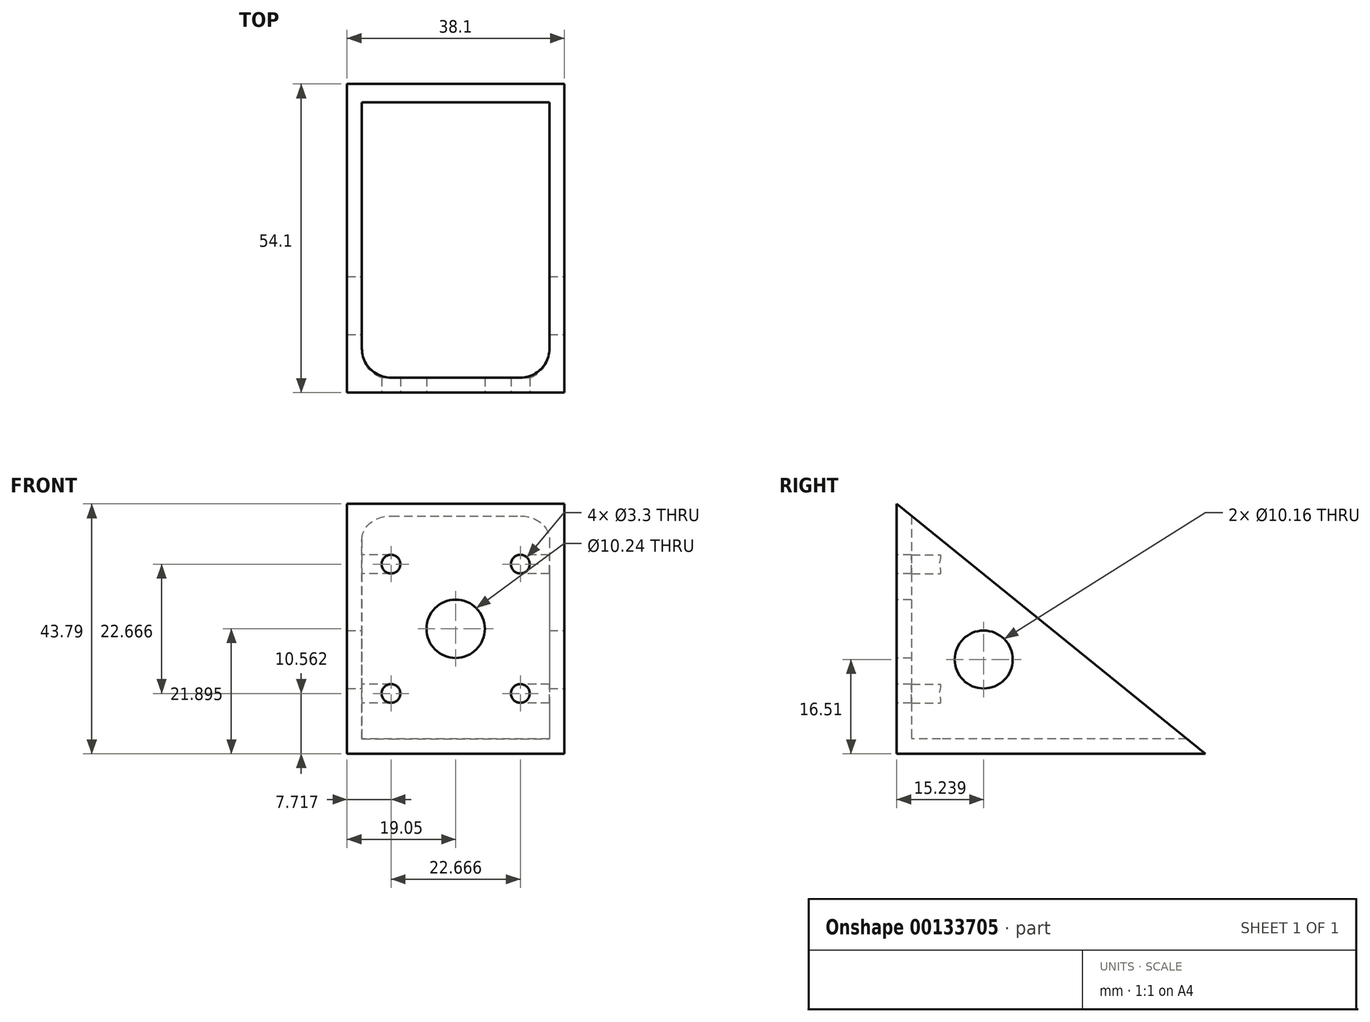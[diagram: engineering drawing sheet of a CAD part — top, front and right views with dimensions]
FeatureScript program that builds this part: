
annotation { "Feature Type Name" : "Feature", "Feature Type Description" : "" }
export const myFeature = defineFeature(function(context is Context, id is Id, definition is map)
    precondition{}
    {
        {
            var Q0;
            Q0=qCreatedBy(makeId("Top.planeOp"),FACE);
            var sketch = newSketch(context, id + "F0", { "sketchPlane" : qUnion([Q0])});
            skLineSegment(sketch, "E0.bottom", {"start": v(19.05, 27.05) * mm, "end": v(-19.05, 27.05) * mm});
            skLineSegment(sketch, "E0.top", {"start": v(19.05, -27.05) * mm, "end": v(-19.05, -27.05) * mm});
            skLineSegment(sketch, "E0.left", {"start": v(19.05, 27.05) * mm, "end": v(19.05, -27.05) * mm});
            skLineSegment(sketch, "E0.right", {"start": v(-19.05, 27.05) * mm, "end": v(-19.05, -27.05) * mm});
            skPoint(sketch, "E0.middle", {"position": v(0, 0) * mm});
            skSolve(sketch);
        }
        {
            var Q0;
            Q0 = qSketchRegion(id + "F0", true);
            extrude(context, id + "F1", {"entities" : qUnion([Q0]), "depth" : 2.6 * mm});
        }
        {
            var Q0;
            Q0=makeQuery(id+"F1.opExtrude","CAP_FACE",FACE,{"disambiguationData":[OSD([sQuery(id+"F0.wireOp",EDGE,"E0.bottom"),sQuery(id+"F0.wireOp",EDGE,"E0.top"),sQuery(id+"F0.wireOp",EDGE,"E0.left"),sQuery(id+"F0.wireOp",EDGE,"E0.right")])],"isStart":false});
            var sketch = newSketch(context, id + "F2", { "sketchPlane" : qUnion([Q0])});
            skLineSegment(sketch, "E1.0", {"start": v(-19.05, 27.05) * mm, "end": v(-19.05, -27.05) * mm});
            skLineSegment(sketch, "E1.1", {"start": v(19.05, -27.05) * mm, "end": v(-19.05, -27.05) * mm});
            skLineSegment(sketch, "E1.2", {"start": v(19.05, 27.05) * mm, "end": v(19.05, -27.05) * mm});
            skLineSegment(sketch, "E2", {"start": v(-19.05, 27.05) * mm, "end": v(-16.43, 27.05) * mm});
            skLineSegment(sketch, "E3", {"start": v(-16.43, 27.05) * mm, "end": v(-16.43, -24.43) * mm});
            skLineSegment(sketch, "E4", {"start": v(-16.43, -24.43) * mm, "end": v(16.43, -24.43) * mm});
            skLineSegment(sketch, "E5", {"start": v(16.43, -24.43) * mm, "end": v(16.43, 27.05) * mm});
            skLineSegment(sketch, "E6", {"start": v(16.43, 27.05) * mm, "end": v(19.05, 27.05) * mm});
            skSolve(sketch);
        }
        {
            var Q0;
            Q0 = qSketchRegion(id + "F2", true);
            extrude(context, id + "F3", {"entities" : qUnion([Q0]), "operationType" : NewBodyOperationType.ADD, "depth" : 41.2 * mm});
        }
        {
            var Q0;
            Q0=makeQuery(id+"F3.boolean.opBoolean","MERGE",FACE,{"derivedFrom":[makeQuery(id+"F1.opExtrude","SWEPT_FACE",FACE,{"disambiguationData":[OSD([sQuery(id+"F0.wireOp",EDGE,"E0.right")])]}),makeQuery(id+"F3.opExtrude","SWEPT_FACE",FACE,{"disambiguationData":[OSD([sQuery(id+"F2.wireOp",EDGE,"E1.0")])]})]});
            var sketch = newSketch(context, id + "F4", { "sketchPlane" : qUnion([Q0])});
            skLineSegment(sketch, "E7", {"start": v(27.05, 43.79) * mm, "end": v(-27.05, 0) * mm});
            skLineSegment(sketch, "E8", {"start": v(-27.05, 0) * mm, "end": v(-42.33, 46.32) * mm});
            skLineSegment(sketch, "E9", {"start": v(-42.33, 46.32) * mm, "end": v(26.03, 63.26) * mm});
            skLineSegment(sketch, "E10", {"start": v(26.03, 63.26) * mm, "end": v(27.05, 43.79) * mm});
            skSolve(sketch);
        }
        {
            var Q0;
            Q0 = qSketchRegion(id + "F4", true);
            extrude(context, id + "F5", {"entities" : qUnion([Q0]), "operationType" : NewBodyOperationType.REMOVE, "oppositeDirection" : true, "depth" : 93.9 * mm});
        }
        {
            var Q0;
            Q0=makeQuery(id+"F3.boolean.opBoolean","MERGE",FACE,{"derivedFrom":[makeQuery(id+"F1.opExtrude","SWEPT_FACE",FACE,{"disambiguationData":[OSD([sQuery(id+"F0.wireOp",EDGE,"E0.left")])]}),makeQuery(id+"F3.opExtrude","SWEPT_FACE",FACE,{"disambiguationData":[OSD([sQuery(id+"F2.wireOp",EDGE,"E1.2")])]})]});
            var sketch = newSketch(context, id + "F6", { "sketchPlane" : qUnion([Q0])});
            skCircle(sketch, "E11", {"center": v(-11.81, 16.51) * mm, "radius": 5.08 * mm});
            skSolve(sketch);
        }
        {
            var Q0;
            Q0 = qSketchRegion(id + "F6", true);
            extrude(context, id + "F7", {"entities" : qUnion([Q0]), "operationType" : NewBodyOperationType.REMOVE, "oppositeDirection" : true, "depth" : 51.52 * mm});
        }
        {
            var Q0;
            Q0=makeQuery(id+"F3.boolean.opBoolean","MERGE",FACE,{"derivedFrom":[makeQuery(id+"F1.opExtrude","SWEPT_FACE",FACE,{"disambiguationData":[OSD([sQuery(id+"F0.wireOp",EDGE,"E0.top")])]}),makeQuery(id+"F3.opExtrude","SWEPT_FACE",FACE,{"disambiguationData":[OSD([sQuery(id+"F2.wireOp",EDGE,"E1.1")])]})]});
            var sketch = newSketch(context, id + "F8", { "sketchPlane" : qUnion([Q0])});
            skCircle(sketch, "E12", {"center": v(-11.33, 33.23) * mm, "radius": 1.65 * mm});
            skCircle(sketch, "E13", {"center": v(-11.33, 10.56) * mm, "radius": 1.65 * mm});
            skCircle(sketch, "E14", {"center": v(11.33, 10.56) * mm, "radius": 1.65 * mm});
            skCircle(sketch, "E15", {"center": v(11.33, 33.23) * mm, "radius": 1.65 * mm});
            skCircle(sketch, "E16", {"center": v(0, 21.9) * mm, "radius": 5.12 * mm});
            skLineSegment(sketch, "E17", {"start": v(-11.33, 33.23) * mm, "end": v(0, 21.9) * mm, "construction": true});
            skLineSegment(sketch, "E18", {"start": v(-11.33, 10.56) * mm, "end": v(0, 21.9) * mm, "construction": true});
            skLineSegment(sketch, "E19", {"start": v(11.33, 10.56) * mm, "end": v(0, 21.9) * mm, "construction": true});
            skLineSegment(sketch, "E20", {"start": v(0, 21.9) * mm, "end": v(11.33, 33.23) * mm, "construction": true});
            skLineSegment(sketch, "E21", {"start": v(-11.33, 33.23) * mm, "end": v(11.33, 33.23) * mm, "construction": true});
            skLineSegment(sketch, "E22", {"start": v(11.33, 10.56) * mm, "end": v(11.33, 33.23) * mm, "construction": true});
            skLineSegment(sketch, "E23", {"start": v(11.33, 10.56) * mm, "end": v(-11.33, 10.56) * mm, "construction": true});
            skLineSegment(sketch, "E24", {"start": v(-11.33, 10.56) * mm, "end": v(-11.33, 33.23) * mm, "construction": true});
            skLineSegment(sketch, "E25", {"start": v(0, 43.79) * mm, "end": v(0, 21.9) * mm, "construction": true});
            skLineSegment(sketch, "E26", {"start": v(0, 21.9) * mm, "end": v(0, 0) * mm, "construction": true});
            skSolve(sketch);
        }
        {
            var Q0;
            Q0 = qSketchRegion(id + "F8", true);
            extrude(context, id + "F9", {"entities" : qUnion([Q0]), "operationType" : NewBodyOperationType.REMOVE, "oppositeDirection" : true, "depth" : 25.4 * mm});
        }
        {
            var Q0;
            Q0=makeQuery(id+"F3.opExtrude","SWEPT_EDGE",EDGE,{"disambiguationData":[OSD([sQuery(id+"F2.wireOp",EDGE,"E4"),sQuery(id+"F2.wireOp",EDGE,"E5")])]});
            var Q1;
            Q1=makeQuery(id+"F3.opExtrude","CAP_EDGE",EDGE,{"disambiguationData":[OSD([sQuery(id+"F2.wireOp",EDGE,"E5")])],"isStart":true});
            var Q2;
            Q2=makeQuery(id+"F3.opExtrude","CAP_EDGE",EDGE,{"disambiguationData":[OSD([sQuery(id+"F2.wireOp",EDGE,"E4")])],"isStart":true});
            var Q3;
            Q3=makeQuery(id+"F3.opExtrude","CAP_EDGE",EDGE,{"disambiguationData":[OSD([sQuery(id+"F2.wireOp",EDGE,"E3")])],"isStart":true});
            var Q4;
            Q4=makeQuery(id+"F3.opExtrude","SWEPT_EDGE",EDGE,{"disambiguationData":[OSD([sQuery(id+"F2.wireOp",EDGE,"E3"),sQuery(id+"F2.wireOp",EDGE,"E4")])]});
            fillet(context, id + "F10", {"entities" : qUnion([Q0, Q1, Q2, Q3, Q4]), "radius" : 5.08 * mm, "tangentPropagation" : true, "allowEdgeOverflow" : false});
        }
    });
